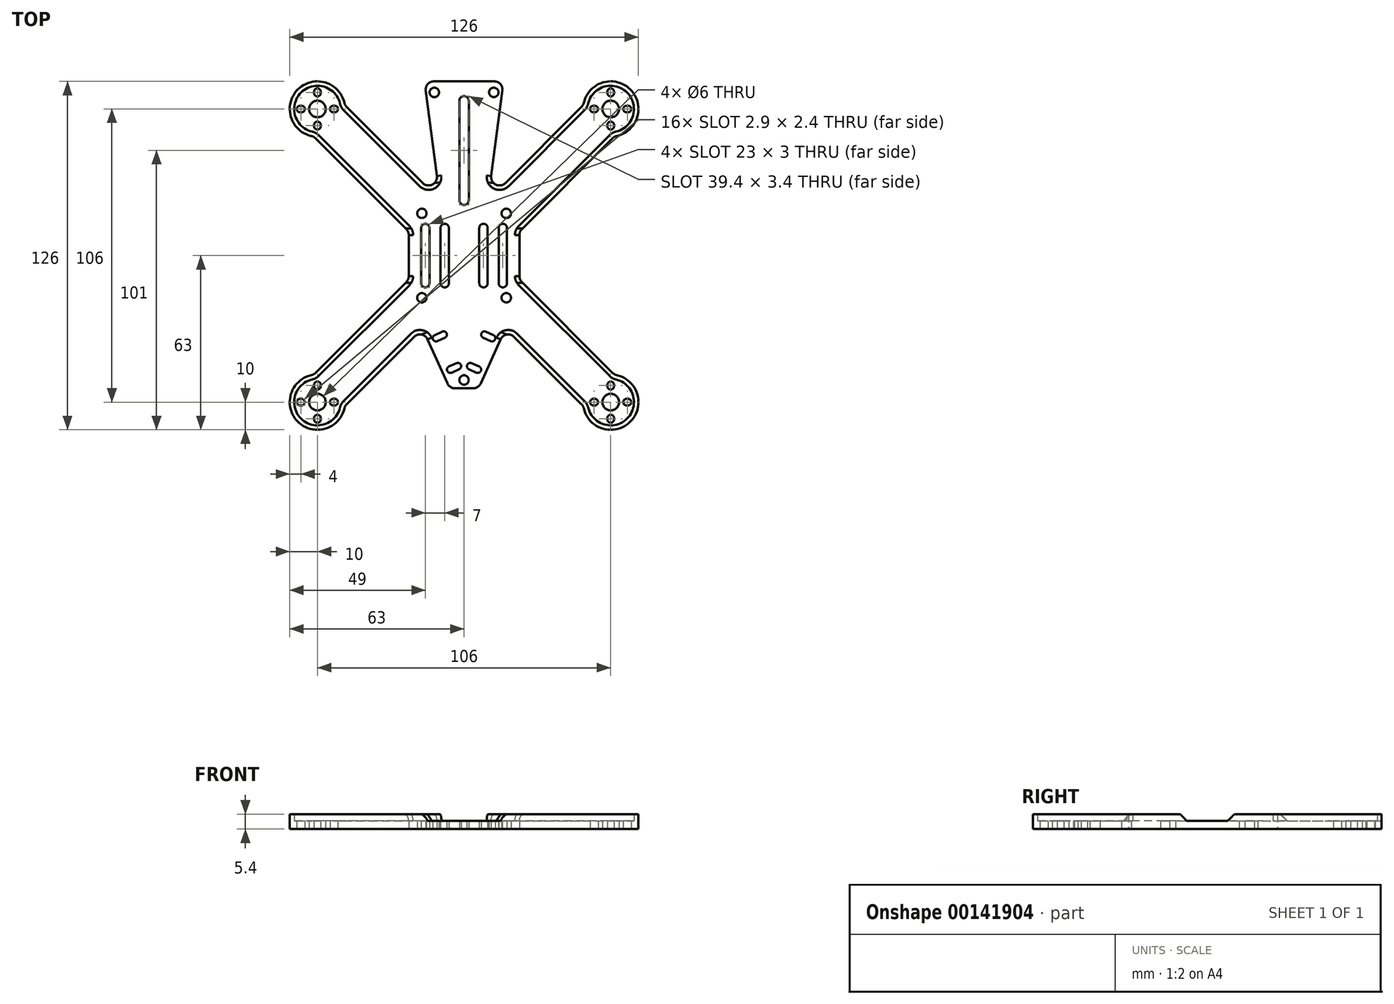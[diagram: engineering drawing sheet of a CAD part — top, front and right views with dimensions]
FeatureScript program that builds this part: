
annotation { "Feature Type Name" : "Feature", "Feature Type Description" : "" }
export const myFeature = defineFeature(function(context is Context, id is Id, definition is map)
    precondition{}
    {
        {
            var Q0;
            Q0=qCreatedBy(makeId("Top.planeOp"),FACE);
            var sketch = newSketch(context, id + "F0", { "sketchPlane" : qUnion([Q0])});
            skCircle(sketch, "E0", {"center": v(15.25, 15.25) * mm, "radius": 1.7 * mm});
            skCircle(sketch, "E1", {"center": v(53, 53) * mm, "radius": 3 * mm});
            skCircle(sketch, "E2", {"center": v(10.75, 59) * mm, "radius": 1.7 * mm});
            skLineSegment(sketch, "E3", {"start": v(0, 0) * mm, "end": v(53, 53) * mm, "construction": true});
            skLineSegment(sketch, "E4", {"start": v(58.75, 53) * mm, "end": v(59.25, 53) * mm, "construction": true});
            skArc(sketch, "E5.0", {"start": v(55.21, 43.25) * mm, "mid": v(60.07, 60.07) * mm, "end": v(43.25, 55.21) * mm});
            skArc(sketch, "E6.0.startCap", {"start": v(58.75, 51.8) * mm, "mid": v(57.55, 53) * mm, "end": v(58.75, 54.2) * mm});
            skArc(sketch, "E6.0.endCap", {"start": v(59.25, 54.2) * mm, "mid": v(60.45, 53) * mm, "end": v(59.25, 51.8) * mm});
            skLineSegment(sketch, "E6.0.left", {"start": v(58.75, 54.2) * mm, "end": v(59.25, 54.2) * mm});
            skLineSegment(sketch, "E6.0.right", {"start": v(58.75, 51.8) * mm, "end": v(59.25, 51.8) * mm});
            skArc(sketch, "E7.1.0", {"start": v(54.2, 58.75) * mm, "mid": v(53, 57.55) * mm, "end": v(51.8, 58.75) * mm});
            skArc(sketch, "E7.1.1", {"start": v(51.8, 59.25) * mm, "mid": v(53, 60.45) * mm, "end": v(54.2, 59.25) * mm});
            skLineSegment(sketch, "E7.1.2", {"start": v(53, 58.75) * mm, "end": v(53, 59.25) * mm, "construction": true});
            skLineSegment(sketch, "E7.1.3", {"start": v(51.8, 58.75) * mm, "end": v(51.8, 59.25) * mm});
            skLineSegment(sketch, "E7.1.4", {"start": v(54.2, 58.75) * mm, "end": v(54.2, 59.25) * mm});
            skArc(sketch, "E7.2.0", {"start": v(47.25, 54.2) * mm, "mid": v(48.45, 53) * mm, "end": v(47.25, 51.8) * mm});
            skArc(sketch, "E7.2.1", {"start": v(46.75, 51.8) * mm, "mid": v(45.55, 53) * mm, "end": v(46.75, 54.2) * mm});
            skLineSegment(sketch, "E7.2.2", {"start": v(47.25, 53) * mm, "end": v(46.75, 53) * mm, "construction": true});
            skLineSegment(sketch, "E7.2.3", {"start": v(47.25, 51.8) * mm, "end": v(46.75, 51.8) * mm});
            skLineSegment(sketch, "E7.2.4", {"start": v(47.25, 54.2) * mm, "end": v(46.75, 54.2) * mm});
            skArc(sketch, "E7.3.0", {"start": v(51.8, 47.25) * mm, "mid": v(53, 48.45) * mm, "end": v(54.2, 47.25) * mm});
            skArc(sketch, "E7.3.1", {"start": v(54.2, 46.75) * mm, "mid": v(53, 45.55) * mm, "end": v(51.8, 46.75) * mm});
            skLineSegment(sketch, "E7.3.2", {"start": v(53, 47.25) * mm, "end": v(53, 46.75) * mm, "construction": true});
            skLineSegment(sketch, "E7.3.3", {"start": v(54.2, 47.25) * mm, "end": v(54.2, 46.75) * mm});
            skLineSegment(sketch, "E7.3.4", {"start": v(51.8, 47.25) * mm, "end": v(51.8, 46.75) * mm});
            skLineSegment(sketch, "E8", {"start": v(0, 20) * mm, "end": v(0, 56) * mm, "construction": true});
            skArc(sketch, "E9.0.startCap", {"start": v(1.7, 20) * mm, "mid": v(0, 18.3) * mm, "end": v(-1.7, 20) * mm});
            skArc(sketch, "E9.0.endCap", {"start": v(-1.7, 56) * mm, "mid": v(0, 57.7) * mm, "end": v(1.7, 56) * mm});
            skLineSegment(sketch, "E9.0.left", {"start": v(-1.7, 20) * mm, "end": v(-1.7, 56) * mm});
            skLineSegment(sketch, "E9.0.right", {"start": v(1.7, 20) * mm, "end": v(1.7, 56) * mm});
            skLineSegment(sketch, "E10", {"start": v(14, 0) * mm, "end": v(14, 10) * mm, "construction": true});
            skLineSegment(sketch, "E11", {"start": v(7, 0) * mm, "end": v(7, 10) * mm, "construction": true});
            skArc(sketch, "E12.0.startCap", {"start": v(8.5, 0) * mm, "mid": v(7, -1.5) * mm, "end": v(5.5, 0) * mm, "construction": true});
            skArc(sketch, "E12.0.endCap", {"start": v(5.5, 10) * mm, "mid": v(7, 11.5) * mm, "end": v(8.5, 10) * mm});
            skLineSegment(sketch, "E12.0.left", {"start": v(5.5, 0) * mm, "end": v(5.5, 10) * mm});
            skLineSegment(sketch, "E12.0.right", {"start": v(8.5, 0) * mm, "end": v(8.5, 10) * mm});
            skArc(sketch, "E12.1.startCap", {"start": v(15.5, 0) * mm, "mid": v(14, -1.5) * mm, "end": v(12.5, 0) * mm, "construction": true});
            skArc(sketch, "E12.1.endCap", {"start": v(12.5, 10) * mm, "mid": v(14, 11.5) * mm, "end": v(15.5, 10) * mm});
            skLineSegment(sketch, "E12.1.left", {"start": v(12.5, 0) * mm, "end": v(12.5, 10) * mm});
            skLineSegment(sketch, "E12.1.right", {"start": v(15.5, 0) * mm, "end": v(15.5, 10) * mm});
            skLineSegment(sketch, "E13", {"start": v(20, 0) * mm, "end": v(20, 7.44) * mm});
            skLineSegment(sketch, "E14.0", {"start": v(20.88, 9.56) * mm, "end": v(53.76, 42.44) * mm});
            skLineSegment(sketch, "E15.MirrorCS", {"start": v(14.92, 26.24) * mm, "end": v(42.44, 53.76) * mm});
            skLineSegment(sketch, "E16", {"start": v(0, 63) * mm, "end": v(10.88, 63) * mm});
            skLineSegment(sketch, "E17", {"start": v(9.83, 28.75) * mm, "end": v(13.86, 59.61) * mm});
            skPoint(sketch, "E18.visualSharp", {"position": v(14.3, 63) * mm});
            skArc(sketch, "E18.filletArc", {"start": v(13.86, 59.61) * mm, "mid": v(13.13, 61.98) * mm, "end": v(10.88, 63) * mm});
            skPoint(sketch, "E19.visualSharp", {"position": v(8.69, 20) * mm});
            skArc(sketch, "E19.filletArc", {"start": v(9.83, 28.75) * mm, "mid": v(11.48, 25.67) * mm, "end": v(14.92, 26.24) * mm});
            skPoint(sketch, "E20.visualSharp", {"position": v(43.1, 54.41) * mm});
            skArc(sketch, "E20.filletArc", {"start": v(42.44, 53.76) * mm, "mid": v(42.95, 54.43) * mm, "end": v(43.25, 55.21) * mm});
            skPoint(sketch, "E21.visualSharp", {"position": v(20, 8.69) * mm});
            skArc(sketch, "E21.filletArc", {"start": v(20.88, 9.56) * mm, "mid": v(20.23, 8.6) * mm, "end": v(20, 7.44) * mm});
            skPoint(sketch, "E22.visualSharp", {"position": v(54.41, 43.1) * mm});
            skArc(sketch, "E22.filletArc", {"start": v(55.21, 43.25) * mm, "mid": v(54.43, 42.95) * mm, "end": v(53.76, 42.44) * mm});
            skArc(sketch, "E23.0", {"start": v(19.75, 10.7) * mm, "mid": v(18.75, 9.2) * mm, "end": v(18.4, 7.44) * mm});
            skLineSegment(sketch, "E23.1", {"start": v(19.75, 10.7) * mm, "end": v(52.63, 43.58) * mm});
            skArc(sketch, "E23.2", {"start": v(54.86, 44.8) * mm, "mid": v(53.66, 44.35) * mm, "end": v(52.63, 43.58) * mm});
            skArc(sketch, "E23.3", {"start": v(8.24, 28.95) * mm, "mid": v(10.77, 24.23) * mm, "end": v(16.06, 25.1) * mm});
            skLineSegment(sketch, "E23.4", {"start": v(16.06, 25.1) * mm, "end": v(43.58, 52.63) * mm});
            skArc(sketch, "E23.5", {"start": v(43.58, 52.63) * mm, "mid": v(44.35, 53.66) * mm, "end": v(44.8, 54.86) * mm});
            skArc(sketch, "E23.6", {"start": v(54.86, 44.8) * mm, "mid": v(58.94, 58.94) * mm, "end": v(44.8, 54.86) * mm});
            skLineSegment(sketch, "E24", {"start": v(9.83, 28.75) * mm, "end": v(8.24, 28.95) * mm});
            skLineSegment(sketch, "E25", {"start": v(20, 7.44) * mm, "end": v(18.4, 7.44) * mm});
            skLineSegment(sketch, "E26.MirrorCS", {"start": v(20.88, -9.56) * mm, "end": v(53.76, -42.44) * mm});
            skLineSegment(sketch, "E27.MirrorCS", {"start": v(19.75, -10.7) * mm, "end": v(52.63, -43.58) * mm});
            skLineSegment(sketch, "E28.MirrorCS", {"start": v(20, -7.44) * mm, "end": v(18.4, -7.44) * mm});
            skArc(sketch, "E29.MirrorCS", {"start": v(20.88, -9.56) * mm, "mid": v(20.23, -8.6) * mm, "end": v(20, -7.44) * mm});
            skArc(sketch, "E30.MirrorCS", {"start": v(19.75, -10.7) * mm, "mid": v(18.75, -9.2) * mm, "end": v(18.4, -7.44) * mm});
            skLineSegment(sketch, "E31.MirrorCS", {"start": v(8.5, 0) * mm, "end": v(8.5, -10) * mm});
            skLineSegment(sketch, "E32.MirrorCS", {"start": v(15.5, 0) * mm, "end": v(15.5, -10) * mm});
            skLineSegment(sketch, "E33.MirrorCS", {"start": v(12.5, 0) * mm, "end": v(12.5, -10) * mm});
            skLineSegment(sketch, "E34.MirrorCS", {"start": v(7, 0) * mm, "end": v(7, -10) * mm, "construction": true});
            skArc(sketch, "E35.MirrorCS", {"start": v(8.5, 0) * mm, "mid": v(7, 1.5) * mm, "end": v(5.5, 0) * mm, "construction": true});
            skLineSegment(sketch, "E36.MirrorCS", {"start": v(20, 0) * mm, "end": v(20, -7.44) * mm});
            skArc(sketch, "E37.MirrorCS", {"start": v(5.5, -10) * mm, "mid": v(7, -11.5) * mm, "end": v(8.5, -10) * mm});
            skLineSegment(sketch, "E38.MirrorCS", {"start": v(5.5, 0) * mm, "end": v(5.5, -10) * mm});
            skPoint(sketch, "E39.MirrorP", {"position": v(20, -8.69) * mm});
            skCircle(sketch, "E40.MirrorC", {"center": v(15.25, -15.25) * mm, "radius": 1.7 * mm});
            skArc(sketch, "E41.MirrorCS", {"start": v(15.5, 0) * mm, "mid": v(14, 1.5) * mm, "end": v(12.5, 0) * mm, "construction": true});
            skLineSegment(sketch, "E42.MirrorCS", {"start": v(14, 0) * mm, "end": v(14, -10) * mm, "construction": true});
            skArc(sketch, "E43.MirrorCS", {"start": v(12.5, -10) * mm, "mid": v(14, -11.5) * mm, "end": v(15.5, -10) * mm});
            skPoint(sketch, "E44.MirrorP", {"position": v(8.69, -20) * mm});
            skLineSegment(sketch, "E45.MirrorCS", {"start": v(58.75, -51.8) * mm, "end": v(59.25, -51.8) * mm});
            skLineSegment(sketch, "E46.MirrorCS", {"start": v(58.75, -54.2) * mm, "end": v(59.25, -54.2) * mm});
            skLineSegment(sketch, "E47.MirrorCS", {"start": v(58.75, -53) * mm, "end": v(59.25, -53) * mm, "construction": true});
            skArc(sketch, "E48.MirrorCS", {"start": v(59.25, -54.2) * mm, "mid": v(60.45, -53) * mm, "end": v(59.25, -51.8) * mm});
            skArc(sketch, "E49.MirrorCS", {"start": v(58.75, -51.8) * mm, "mid": v(57.55, -53) * mm, "end": v(58.75, -54.2) * mm});
            skArc(sketch, "E50.MirrorCS", {"start": v(51.8, -59.25) * mm, "mid": v(53, -60.45) * mm, "end": v(54.2, -59.25) * mm});
            skLineSegment(sketch, "E51.MirrorCS", {"start": v(53, -58.75) * mm, "end": v(53, -59.25) * mm, "construction": true});
            skArc(sketch, "E52.MirrorCS", {"start": v(42.44, -53.76) * mm, "mid": v(42.95, -54.43) * mm, "end": v(43.25, -55.21) * mm});
            skLineSegment(sketch, "E53.MirrorCS", {"start": v(51.8, -58.75) * mm, "end": v(51.8, -59.25) * mm});
            skLineSegment(sketch, "E54.MirrorCS", {"start": v(51.8, -47.25) * mm, "end": v(51.8, -46.75) * mm});
            skLineSegment(sketch, "E55.MirrorCS", {"start": v(53, -47.25) * mm, "end": v(53, -46.75) * mm, "construction": true});
            skLineSegment(sketch, "E56.MirrorCS", {"start": v(47.25, -53) * mm, "end": v(46.75, -53) * mm, "construction": true});
            skArc(sketch, "E57.MirrorCS", {"start": v(55.21, -43.25) * mm, "mid": v(54.43, -42.95) * mm, "end": v(53.76, -42.44) * mm});
            skLineSegment(sketch, "E58.MirrorCS", {"start": v(47.25, -54.2) * mm, "end": v(46.75, -54.2) * mm});
            skArc(sketch, "E59.MirrorCS", {"start": v(43.58, -52.63) * mm, "mid": v(44.35, -53.66) * mm, "end": v(44.8, -54.86) * mm});
            skLineSegment(sketch, "E60.MirrorCS", {"start": v(54.2, -47.25) * mm, "end": v(54.2, -46.75) * mm});
            skLineSegment(sketch, "E61.MirrorCS", {"start": v(54.2, -58.75) * mm, "end": v(54.2, -59.25) * mm});
            skArc(sketch, "E62.MirrorCS", {"start": v(47.25, -54.2) * mm, "mid": v(48.45, -53) * mm, "end": v(47.25, -51.8) * mm});
            skLineSegment(sketch, "E63.MirrorCS", {"start": v(47.25, -51.8) * mm, "end": v(46.75, -51.8) * mm});
            skArc(sketch, "E64.MirrorCS", {"start": v(54.86, -44.8) * mm, "mid": v(53.66, -44.35) * mm, "end": v(52.63, -43.58) * mm});
            skArc(sketch, "E65.MirrorCS", {"start": v(54.2, -46.75) * mm, "mid": v(53, -45.55) * mm, "end": v(51.8, -46.75) * mm});
            skArc(sketch, "E66.MirrorCS", {"start": v(54.2, -58.75) * mm, "mid": v(53, -57.55) * mm, "end": v(51.8, -58.75) * mm});
            skPoint(sketch, "E67.MirrorP", {"position": v(43.1, -54.41) * mm});
            skArc(sketch, "E68.MirrorCS", {"start": v(46.75, -51.8) * mm, "mid": v(45.55, -53) * mm, "end": v(46.75, -54.2) * mm});
            skArc(sketch, "E69.MirrorCS", {"start": v(54.86, -44.8) * mm, "mid": v(58.94, -58.94) * mm, "end": v(44.8, -54.86) * mm});
            skArc(sketch, "E70.MirrorCS", {"start": v(51.8, -47.25) * mm, "mid": v(53, -48.45) * mm, "end": v(54.2, -47.25) * mm});
            skPoint(sketch, "E71.MirrorP", {"position": v(54.41, -43.1) * mm});
            skArc(sketch, "E72.MirrorCS", {"start": v(55.21, -43.25) * mm, "mid": v(60.07, -60.07) * mm, "end": v(43.25, -55.21) * mm});
            skCircle(sketch, "E73.MirrorC", {"center": v(53, -53) * mm, "radius": 3 * mm});
            skLineSegment(sketch, "E74", {"start": v(42.44, -53.76) * mm, "end": v(18.07, -29.39) * mm});
            skCircle(sketch, "E75", {"center": v(0, -45) * mm, "radius": 1.7 * mm});
            skLineSegment(sketch, "E76", {"start": v(0, -48) * mm, "end": v(3.3, -48) * mm});
            skLineSegment(sketch, "E77", {"start": v(6.03, -46.23) * mm, "end": v(13.22, -30.27) * mm});
            skPoint(sketch, "E78.visualSharp", {"position": v(5.23, -48) * mm});
            skArc(sketch, "E78.filletArc", {"start": v(3.3, -48) * mm, "mid": v(4.92, -47.52) * mm, "end": v(6.03, -46.23) * mm});
            skPoint(sketch, "E79.visualSharp", {"position": v(15, -26.31) * mm});
            skArc(sketch, "E79.filletArc", {"start": v(18.07, -29.39) * mm, "mid": v(15.41, -28.56) * mm, "end": v(13.22, -30.27) * mm});
            skArc(sketch, "E80.0", {"start": v(19.2, -28.25) * mm, "mid": v(15.12, -26.98) * mm, "end": v(11.76, -29.62) * mm});
            skLineSegment(sketch, "E80.1", {"start": v(43.58, -52.63) * mm, "end": v(19.2, -28.25) * mm});
            skLineSegment(sketch, "E81", {"start": v(11.76, -29.62) * mm, "end": v(13.22, -30.27) * mm});
            skLineSegment(sketch, "E82", {"start": v(4.99, -41.23) * mm, "end": v(2.25, -40) * mm, "construction": true});
            skLineSegment(sketch, "E83", {"start": v(10.12, -29.84) * mm, "end": v(7.39, -28.6) * mm, "construction": true});
            skArc(sketch, "E84.0.startCap", {"start": v(10.62, -28.74) * mm, "mid": v(11.22, -30.33) * mm, "end": v(9.63, -30.93) * mm});
            skArc(sketch, "E84.0.endCap", {"start": v(6.9, -29.7) * mm, "mid": v(6.3, -28.11) * mm, "end": v(7.88, -27.5) * mm});
            skLineSegment(sketch, "E84.0.left", {"start": v(9.63, -30.93) * mm, "end": v(6.9, -29.7) * mm});
            skLineSegment(sketch, "E84.0.right", {"start": v(10.62, -28.74) * mm, "end": v(7.88, -27.5) * mm});
            skArc(sketch, "E84.1.startCap", {"start": v(5.48, -40.14) * mm, "mid": v(6.08, -41.73) * mm, "end": v(4.5, -42.33) * mm});
            skArc(sketch, "E84.1.endCap", {"start": v(1.76, -41.1) * mm, "mid": v(1.16, -39.5) * mm, "end": v(2.75, -38.9) * mm});
            skLineSegment(sketch, "E84.1.left", {"start": v(4.5, -42.33) * mm, "end": v(1.76, -41.1) * mm});
            skLineSegment(sketch, "E84.1.right", {"start": v(5.48, -40.14) * mm, "end": v(2.75, -38.9) * mm});
            skLineSegment(sketch, "E85.MirrorCS", {"start": v(-58.75, -51.8) * mm, "end": v(-59.25, -51.8) * mm});
            skLineSegment(sketch, "E86.MirrorCS", {"start": v(-58.75, 53) * mm, "end": v(-59.25, 53) * mm, "construction": true});
            skArc(sketch, "E87.MirrorCS", {"start": v(-58.75, 51.8) * mm, "mid": v(-57.55, 53) * mm, "end": v(-58.75, 54.2) * mm});
            skArc(sketch, "E88.MirrorCS", {"start": v(-59.25, 54.2) * mm, "mid": v(-60.45, 53) * mm, "end": v(-59.25, 51.8) * mm});
            skLineSegment(sketch, "E89.MirrorCS", {"start": v(-58.75, 54.2) * mm, "end": v(-59.25, 54.2) * mm});
            skLineSegment(sketch, "E90.MirrorCS", {"start": v(-58.75, 51.8) * mm, "end": v(-59.25, 51.8) * mm});
            skLineSegment(sketch, "E91.MirrorCS", {"start": v(-58.75, -54.2) * mm, "end": v(-59.25, -54.2) * mm});
            skLineSegment(sketch, "E92.MirrorCS", {"start": v(-54.2, -58.75) * mm, "end": v(-54.2, -59.25) * mm});
            skLineSegment(sketch, "E93.MirrorCS", {"start": v(-58.75, -53) * mm, "end": v(-59.25, -53) * mm, "construction": true});
            skLineSegment(sketch, "E94.MirrorCS", {"start": v(-51.8, -58.75) * mm, "end": v(-51.8, -59.25) * mm});
            skArc(sketch, "E95.MirrorCS", {"start": v(-59.25, -54.2) * mm, "mid": v(-60.45, -53) * mm, "end": v(-59.25, -51.8) * mm});
            skArc(sketch, "E96.MirrorCS", {"start": v(-58.75, -51.8) * mm, "mid": v(-57.55, -53) * mm, "end": v(-58.75, -54.2) * mm});
            skLineSegment(sketch, "E97.MirrorCS", {"start": v(-53, -58.75) * mm, "end": v(-53, -59.25) * mm, "construction": true});
            skArc(sketch, "E98.MirrorCS", {"start": v(-54.2, -58.75) * mm, "mid": v(-53, -57.55) * mm, "end": v(-51.8, -58.75) * mm});
            skArc(sketch, "E99.MirrorCS", {"start": v(-51.8, 47.25) * mm, "mid": v(-53, 48.45) * mm, "end": v(-54.2, 47.25) * mm});
            skArc(sketch, "E100.MirrorCS", {"start": v(-54.2, 46.75) * mm, "mid": v(-53, 45.55) * mm, "end": v(-51.8, 46.75) * mm});
            skLineSegment(sketch, "E101.MirrorCS", {"start": v(-53, 47.25) * mm, "end": v(-53, 46.75) * mm, "construction": true});
            skLineSegment(sketch, "E102.MirrorCS", {"start": v(-54.2, 47.25) * mm, "end": v(-54.2, 46.75) * mm});
            skLineSegment(sketch, "E103.MirrorCS", {"start": v(-51.8, 58.75) * mm, "end": v(-51.8, 59.25) * mm});
            skLineSegment(sketch, "E104.MirrorCS", {"start": v(-54.2, 58.75) * mm, "end": v(-54.2, 59.25) * mm});
            skLineSegment(sketch, "E105.MirrorCS", {"start": v(-51.8, 47.25) * mm, "end": v(-51.8, 46.75) * mm});
            skLineSegment(sketch, "E106.MirrorCS", {"start": v(-47.25, -54.2) * mm, "end": v(-46.75, -54.2) * mm});
            skArc(sketch, "E107.MirrorCS", {"start": v(-51.8, -59.25) * mm, "mid": v(-53, -60.45) * mm, "end": v(-54.2, -59.25) * mm});
            skArc(sketch, "E108.MirrorCS", {"start": v(-46.75, -51.8) * mm, "mid": v(-45.55, -53) * mm, "end": v(-46.75, -54.2) * mm});
            skLineSegment(sketch, "E109.MirrorCS", {"start": v(-47.25, 54.2) * mm, "end": v(-46.75, 54.2) * mm});
            skLineSegment(sketch, "E110.MirrorCS", {"start": v(-47.25, -51.8) * mm, "end": v(-46.75, -51.8) * mm});
            skLineSegment(sketch, "E111.MirrorCS", {"start": v(-47.25, -53) * mm, "end": v(-46.75, -53) * mm, "construction": true});
            skArc(sketch, "E112.MirrorCS", {"start": v(-54.2, 58.75) * mm, "mid": v(-53, 57.55) * mm, "end": v(-51.8, 58.75) * mm});
            skArc(sketch, "E113.MirrorCS", {"start": v(-51.8, 59.25) * mm, "mid": v(-53, 60.45) * mm, "end": v(-54.2, 59.25) * mm});
            skLineSegment(sketch, "E114.MirrorCS", {"start": v(-53, 58.75) * mm, "end": v(-53, 59.25) * mm, "construction": true});
            skArc(sketch, "E115.MirrorCS", {"start": v(-47.25, -54.2) * mm, "mid": v(-48.45, -53) * mm, "end": v(-47.25, -51.8) * mm});
            skLineSegment(sketch, "E116.MirrorCS", {"start": v(-47.25, 51.8) * mm, "end": v(-46.75, 51.8) * mm});
            skArc(sketch, "E117.MirrorCS", {"start": v(-20.88, -9.56) * mm, "mid": v(-20.23, -8.6) * mm, "end": v(-20, -7.44) * mm});
            skArc(sketch, "E118.MirrorCS", {"start": v(-8.5, 0) * mm, "mid": v(-7, 1.5) * mm, "end": v(-5.5, 0) * mm, "construction": true});
            skArc(sketch, "E119.MirrorCS", {"start": v(-15.5, 0) * mm, "mid": v(-14, -1.5) * mm, "end": v(-12.5, 0) * mm, "construction": true});
            skArc(sketch, "E120.MirrorCS", {"start": v(-47.25, 54.2) * mm, "mid": v(-48.45, 53) * mm, "end": v(-47.25, 51.8) * mm});
            skArc(sketch, "E121.MirrorCS", {"start": v(-15.5, 0) * mm, "mid": v(-14, 1.5) * mm, "end": v(-12.5, 0) * mm, "construction": true});
            skLineSegment(sketch, "E122.MirrorCS", {"start": v(-20, 7.44) * mm, "end": v(-18.4, 7.44) * mm});
            skArc(sketch, "E123.MirrorCS", {"start": v(-46.75, 51.8) * mm, "mid": v(-45.55, 53) * mm, "end": v(-46.75, 54.2) * mm});
            skLineSegment(sketch, "E124.MirrorCS", {"start": v(-20, -7.44) * mm, "end": v(-18.4, -7.44) * mm});
            skArc(sketch, "E125.MirrorCS", {"start": v(-20.88, 9.56) * mm, "mid": v(-20.23, 8.6) * mm, "end": v(-20, 7.44) * mm});
            skArc(sketch, "E126.MirrorCS", {"start": v(-8.5, 0) * mm, "mid": v(-7, -1.5) * mm, "end": v(-5.5, 0) * mm, "construction": true});
            skLineSegment(sketch, "E127.MirrorCS", {"start": v(-47.25, 53) * mm, "end": v(-46.75, 53) * mm, "construction": true});
            skArc(sketch, "E128.MirrorCS", {"start": v(-10.62, -28.74) * mm, "mid": v(-11.22, -30.33) * mm, "end": v(-9.63, -30.93) * mm});
            skArc(sketch, "E129.MirrorCS", {"start": v(-19.75, 10.7) * mm, "mid": v(-18.75, 9.2) * mm, "end": v(-18.4, 7.44) * mm});
            skLineSegment(sketch, "E130.MirrorCS", {"start": v(-10.12, -29.84) * mm, "end": v(-7.39, -28.6) * mm, "construction": true});
            skArc(sketch, "E131.MirrorCS", {"start": v(-55.21, 43.25) * mm, "mid": v(-54.43, 42.95) * mm, "end": v(-53.76, 42.44) * mm});
            skArc(sketch, "E132.MirrorCS", {"start": v(-42.44, -53.76) * mm, "mid": v(-42.95, -54.43) * mm, "end": v(-43.25, -55.21) * mm});
            skArc(sketch, "E133.MirrorCS", {"start": v(-6.9, -29.7) * mm, "mid": v(-6.3, -28.11) * mm, "end": v(-7.88, -27.5) * mm});
            skArc(sketch, "E134.MirrorCS", {"start": v(-54.86, 44.8) * mm, "mid": v(-53.66, 44.35) * mm, "end": v(-52.63, 43.58) * mm});
            skLineSegment(sketch, "E135.MirrorCS", {"start": v(-9.63, -30.93) * mm, "end": v(-6.9, -29.7) * mm});
            skArc(sketch, "E136.MirrorCS", {"start": v(-51.8, -47.25) * mm, "mid": v(-53, -48.45) * mm, "end": v(-54.2, -47.25) * mm});
            skLineSegment(sketch, "E137.MirrorCS", {"start": v(-51.8, -47.25) * mm, "end": v(-51.8, -46.75) * mm});
            skLineSegment(sketch, "E138.MirrorCS", {"start": v(-10.62, -28.74) * mm, "end": v(-7.88, -27.5) * mm});
            skArc(sketch, "E139.MirrorCS", {"start": v(-42.44, 53.76) * mm, "mid": v(-42.95, 54.43) * mm, "end": v(-43.25, 55.21) * mm});
            skLineSegment(sketch, "E140.MirrorCS", {"start": v(-11.76, -29.62) * mm, "end": v(-13.22, -30.27) * mm});
            skLineSegment(sketch, "E141.MirrorCS", {"start": v(-53, -47.25) * mm, "end": v(-53, -46.75) * mm, "construction": true});
            skArc(sketch, "E142.MirrorCS", {"start": v(-5.48, -40.14) * mm, "mid": v(-6.08, -41.73) * mm, "end": v(-4.5, -42.33) * mm});
            skArc(sketch, "E143.MirrorCS", {"start": v(-54.86, -44.8) * mm, "mid": v(-53.66, -44.35) * mm, "end": v(-52.63, -43.58) * mm});
            skArc(sketch, "E144.MirrorCS", {"start": v(-55.21, -43.25) * mm, "mid": v(-54.43, -42.95) * mm, "end": v(-53.76, -42.44) * mm});
            skLineSegment(sketch, "E145.MirrorCS", {"start": v(-9.83, 28.75) * mm, "end": v(-8.24, 28.95) * mm});
            skArc(sketch, "E146.MirrorCS", {"start": v(-54.2, -46.75) * mm, "mid": v(-53, -45.55) * mm, "end": v(-51.8, -46.75) * mm});
            skLineSegment(sketch, "E147.MirrorCS", {"start": v(-54.2, -47.25) * mm, "end": v(-54.2, -46.75) * mm});
            skArc(sketch, "E148.MirrorCS", {"start": v(-19.75, -10.7) * mm, "mid": v(-18.75, -9.2) * mm, "end": v(-18.4, -7.44) * mm});
            skArc(sketch, "E149.MirrorCS", {"start": v(-43.58, 52.63) * mm, "mid": v(-44.35, 53.66) * mm, "end": v(-44.8, 54.86) * mm});
            skArc(sketch, "E150.MirrorCS", {"start": v(-1.76, -41.1) * mm, "mid": v(-1.16, -39.5) * mm, "end": v(-2.75, -38.9) * mm});
            skCircle(sketch, "E151.MirrorC", {"center": v(-10.75, 59) * mm, "radius": 1.7 * mm});
            skLineSegment(sketch, "E152.MirrorCS", {"start": v(-4.5, -42.33) * mm, "end": v(-1.76, -41.1) * mm});
            skLineSegment(sketch, "E153.MirrorCS", {"start": v(-5.48, -40.14) * mm, "end": v(-2.75, -38.9) * mm});
            skArc(sketch, "E154.MirrorCS", {"start": v(-1.7, 20) * mm, "mid": v(0, 18.3) * mm, "end": v(1.7, 20) * mm});
            skArc(sketch, "E155.MirrorCS", {"start": v(-43.58, -52.63) * mm, "mid": v(-44.35, -53.66) * mm, "end": v(-44.8, -54.86) * mm});
            skLineSegment(sketch, "E156.MirrorCS", {"start": v(-4.99, -41.23) * mm, "end": v(-2.25, -40) * mm, "construction": true});
            skArc(sketch, "E157.MirrorCS", {"start": v(1.7, 56) * mm, "mid": v(0, 57.7) * mm, "end": v(-1.7, 56) * mm});
            skArc(sketch, "E158.MirrorCS", {"start": v(-3.3, -48) * mm, "mid": v(-4.92, -47.52) * mm, "end": v(-6.03, -46.23) * mm});
            skArc(sketch, "E159.MirrorCS", {"start": v(-9.83, 28.75) * mm, "mid": v(-11.48, 25.67) * mm, "end": v(-14.92, 26.24) * mm});
            skArc(sketch, "E160.MirrorCS", {"start": v(-8.24, 28.95) * mm, "mid": v(-10.77, 24.23) * mm, "end": v(-16.06, 25.1) * mm});
            skArc(sketch, "E161.MirrorCS", {"start": v(-12.5, 10) * mm, "mid": v(-14, 11.5) * mm, "end": v(-15.5, 10) * mm});
            skCircle(sketch, "E162.MirrorC", {"center": v(-15.25, 15.25) * mm, "radius": 1.7 * mm});
            skLineSegment(sketch, "E163.MirrorCS", {"start": v(0, -48) * mm, "end": v(-3.3, -48) * mm});
            skArc(sketch, "E164.MirrorCS", {"start": v(-13.86, 59.61) * mm, "mid": v(-13.13, 61.98) * mm, "end": v(-10.88, 63) * mm});
            skArc(sketch, "E165.MirrorCS", {"start": v(-19.2, -28.25) * mm, "mid": v(-15.12, -26.98) * mm, "end": v(-11.76, -29.62) * mm});
            skLineSegment(sketch, "E166.MirrorCS", {"start": v(-5.5, 0) * mm, "end": v(-5.5, 10) * mm});
            skLineSegment(sketch, "E167.MirrorCS", {"start": v(-12.5, 0) * mm, "end": v(-12.5, -10) * mm});
            skPoint(sketch, "E168.MirrorP", {"position": v(-8.69, -20) * mm});
            skPoint(sketch, "E169.MirrorP", {"position": v(-53, -53) * mm});
            skArc(sketch, "E170.MirrorCS", {"start": v(-5.5, 10) * mm, "mid": v(-7, 11.5) * mm, "end": v(-8.5, 10) * mm});
            skLineSegment(sketch, "E171.MirrorCS", {"start": v(-15.5, 0) * mm, "end": v(-15.5, -10) * mm});
            skPoint(sketch, "E172.MirrorP", {"position": v(-54.41, 43.1) * mm});
            skPoint(sketch, "E173.MirrorP", {"position": v(-20, -8.69) * mm});
            skLineSegment(sketch, "E174.MirrorCS", {"start": v(-19.75, -10.7) * mm, "end": v(-52.63, -43.58) * mm});
            skLineSegment(sketch, "E175.MirrorCS", {"start": v(-9.83, 28.75) * mm, "end": v(-13.86, 59.61) * mm});
            skArc(sketch, "E176.MirrorCS", {"start": v(-18.07, -29.39) * mm, "mid": v(-15.41, -28.56) * mm, "end": v(-13.22, -30.27) * mm});
            skLineSegment(sketch, "E177.MirrorCS", {"start": v(-7, 0) * mm, "end": v(-7, -10) * mm, "construction": true});
            skLineSegment(sketch, "E178.MirrorCS", {"start": v(-19.75, 10.7) * mm, "end": v(-52.63, 43.58) * mm});
            skLineSegment(sketch, "E179.MirrorCS", {"start": v(-8.5, 0) * mm, "end": v(-8.5, 10) * mm});
            skArc(sketch, "E180.MirrorCS", {"start": v(-54.86, -44.8) * mm, "mid": v(-58.94, -58.94) * mm, "end": v(-44.8, -54.86) * mm});
            skLineSegment(sketch, "E181.MirrorCS", {"start": v(-14, 0) * mm, "end": v(-14, 10) * mm, "construction": true});
            skPoint(sketch, "E182.MirrorP", {"position": v(-53, 53) * mm});
            skLineSegment(sketch, "E183.MirrorCS", {"start": v(-43.58, -52.63) * mm, "end": v(-19.2, -28.25) * mm});
            skPoint(sketch, "E184.MirrorP", {"position": v(-43.1, 54.41) * mm});
            skLineSegment(sketch, "E185.MirrorCS", {"start": v(-20, 0) * mm, "end": v(-20, -7.44) * mm});
            skArc(sketch, "E186.MirrorCS", {"start": v(-55.21, -43.25) * mm, "mid": v(-60.07, -60.07) * mm, "end": v(-43.25, -55.21) * mm});
            skLineSegment(sketch, "E187.MirrorCS", {"start": v(-7, 0) * mm, "end": v(-7, 10) * mm, "construction": true});
            skPoint(sketch, "E188.MirrorP", {"position": v(-5.23, -48) * mm});
            skArc(sketch, "E189.MirrorCS", {"start": v(-5.5, -10) * mm, "mid": v(-7, -11.5) * mm, "end": v(-8.5, -10) * mm});
            skLineSegment(sketch, "E190.MirrorCS", {"start": v(-16.06, 25.1) * mm, "end": v(-43.58, 52.63) * mm});
            skCircle(sketch, "E191.MirrorC", {"center": v(-53, -53) * mm, "radius": 3 * mm});
            skLineSegment(sketch, "E192.MirrorCS", {"start": v(-12.5, 0) * mm, "end": v(-12.5, 10) * mm});
            skLineSegment(sketch, "E193.MirrorCS", {"start": v(-15.5, 0) * mm, "end": v(-15.5, 10) * mm});
            skLineSegment(sketch, "E194.MirrorCS", {"start": v(-42.44, -53.76) * mm, "end": v(-18.07, -29.39) * mm});
            skLineSegment(sketch, "E195.MirrorCS", {"start": v(-5.5, 0) * mm, "end": v(-5.5, -10) * mm});
            skCircle(sketch, "E196.MirrorC", {"center": v(-53, 53) * mm, "radius": 3 * mm});
            skPoint(sketch, "E197.MirrorP", {"position": v(-15, -26.31) * mm});
            skLineSegment(sketch, "E198.MirrorCS", {"start": v(0, 0) * mm, "end": v(-53, 53) * mm, "construction": true});
            skArc(sketch, "E199.MirrorCS", {"start": v(-54.86, 44.8) * mm, "mid": v(-58.94, 58.94) * mm, "end": v(-44.8, 54.86) * mm});
            skLineSegment(sketch, "E200.MirrorCS", {"start": v(-20, 0) * mm, "end": v(-20, 7.44) * mm});
            skArc(sketch, "E201.MirrorCS", {"start": v(-55.21, 43.25) * mm, "mid": v(-60.07, 60.07) * mm, "end": v(-43.25, 55.21) * mm});
            skCircle(sketch, "E202.MirrorC", {"center": v(-15.25, -15.25) * mm, "radius": 1.7 * mm});
            skLineSegment(sketch, "E203.MirrorCS", {"start": v(-20.88, 9.56) * mm, "end": v(-53.76, 42.44) * mm});
            skLineSegment(sketch, "E204.MirrorCS", {"start": v(-14, 0) * mm, "end": v(-14, -10) * mm, "construction": true});
            skLineSegment(sketch, "E205.MirrorCS", {"start": v(-14.92, 26.24) * mm, "end": v(-42.44, 53.76) * mm});
            skLineSegment(sketch, "E206.MirrorCS", {"start": v(-6.03, -46.23) * mm, "end": v(-13.22, -30.27) * mm});
            skPoint(sketch, "E207.MirrorP", {"position": v(-8.69, 20) * mm});
            skPoint(sketch, "E208.MirrorP", {"position": v(-43.1, -54.41) * mm});
            skLineSegment(sketch, "E209.MirrorCS", {"start": v(-20.88, -9.56) * mm, "end": v(-53.76, -42.44) * mm});
            skLineSegment(sketch, "E210.MirrorCS", {"start": v(0, 63) * mm, "end": v(-10.88, 63) * mm});
            skArc(sketch, "E211.MirrorCS", {"start": v(-12.5, -10) * mm, "mid": v(-14, -11.5) * mm, "end": v(-15.5, -10) * mm});
            skLineSegment(sketch, "E212.MirrorCS", {"start": v(-8.5, 0) * mm, "end": v(-8.5, -10) * mm});
            skPoint(sketch, "E213.MirrorP", {"position": v(-14.3, 63) * mm});
            skPoint(sketch, "E214.MirrorP", {"position": v(-20, 8.69) * mm});
            skPoint(sketch, "E215.MirrorP", {"position": v(-54.41, -43.1) * mm});
            skLineSegment(sketch, "E216", {"start": v(-53, 53) * mm, "end": v(-23.7, 77.82) * mm, "construction": true});
            skSolve(sketch);
        }
        {
            var Q0;
            Q0=makeQuery(id+"F0.imprint","IMPRINT",FACE,{"disambiguationData":[TD([[makeQuery(id+"F0.imprint","IMPRINT",EDGE,{"derivedFrom":sQuery(id+"F0.wireOp",EDGE,"E0")}),-1.0]])]});
            extrude(context, id + "F1", {"entities" : qUnion([Q0]), "depth" : 3 * mm});
        }
        {
            var Q0;
            Q0=makeQuery(id+"F0.imprint","IMPRINT",FACE,{"disambiguationData":[TD([[makeQuery(id+"F0.imprint","IMPRINT",EDGE,{"derivedFrom":sQuery(id+"F0.wireOp",EDGE,"E122.MirrorCS")}),1.0]])]});
            var Q1;
            Q1=makeQuery(id+"F0.imprint","IMPRINT",FACE,{"disambiguationData":[TD([[makeQuery(id+"F0.imprint","IMPRINT",EDGE,{"derivedFrom":sQuery(id+"F0.wireOp",EDGE,"E5.0")}),1.0]])]});
            var Q2;
            Q2=makeQuery(id+"F0.imprint","IMPRINT",FACE,{"disambiguationData":[TD([[makeQuery(id+"F0.imprint","IMPRINT",EDGE,{"derivedFrom":sQuery(id+"F0.wireOp",EDGE,"E26.MirrorCS")}),-1.0]])]});
            var Q3;
            Q3=makeQuery(id+"F0.imprint","IMPRINT",FACE,{"disambiguationData":[TD([[makeQuery(id+"F0.imprint","IMPRINT",EDGE,{"derivedFrom":sQuery(id+"F0.wireOp",EDGE,"E117.MirrorCS")}),-1.0]])]});
            extrude(context, id + "F2", {"entities" : qUnion([Q0, Q1, Q2, Q3]), "operationType" : NewBodyOperationType.ADD, "depth" : 5.4 * mm});
        }
        {
            var Q0;
            Q0=makeQuery(id+"F2.opExtrude","CAP_EDGE",EDGE,{"disambiguationData":[OSD([sQuery(id+"F0.wireOp",EDGE,"E145.MirrorCS")])],"isStart":false});
            var Q1;
            Q1=makeQuery(id+"F2.opExtrude","CAP_EDGE",EDGE,{"disambiguationData":[OSD([sQuery(id+"F0.wireOp",EDGE,"E122.MirrorCS")])],"isStart":false});
            var Q2;
            Q2=makeQuery(id+"F2.opExtrude","CAP_EDGE",EDGE,{"disambiguationData":[OSD([sQuery(id+"F0.wireOp",EDGE,"E124.MirrorCS")])],"isStart":false});
            var Q3;
            Q3=makeQuery(id+"F2.opExtrude","CAP_EDGE",EDGE,{"disambiguationData":[OSD([sQuery(id+"F0.wireOp",EDGE,"E28.MirrorCS")])],"isStart":false});
            var Q4;
            Q4=makeQuery(id+"F2.opExtrude","CAP_EDGE",EDGE,{"disambiguationData":[OSD([sQuery(id+"F0.wireOp",EDGE,"E25")])],"isStart":false});
            var Q5;
            Q5=makeQuery(id+"F2.opExtrude","CAP_EDGE",EDGE,{"disambiguationData":[OSD([sQuery(id+"F0.wireOp",EDGE,"E24")])],"isStart":false});
            var Q6;
            Q6=makeQuery(id+"F2.opExtrude","CAP_EDGE",EDGE,{"disambiguationData":[OSD([sQuery(id+"F0.wireOp",EDGE,"E81")])],"isStart":false});
            var Q7;
            Q7=makeQuery(id+"F2.opExtrude","CAP_EDGE",EDGE,{"disambiguationData":[OSD([sQuery(id+"F0.wireOp",EDGE,"E140.MirrorCS")])],"isStart":false});
            chamfer(context, id + "F3", {"entities" : qUnion([Q0, Q1, Q2, Q3, Q4, Q5, Q6, Q7]), "width" : 2.4 * mm, "tangentPropagation" : true});
        }
    });
